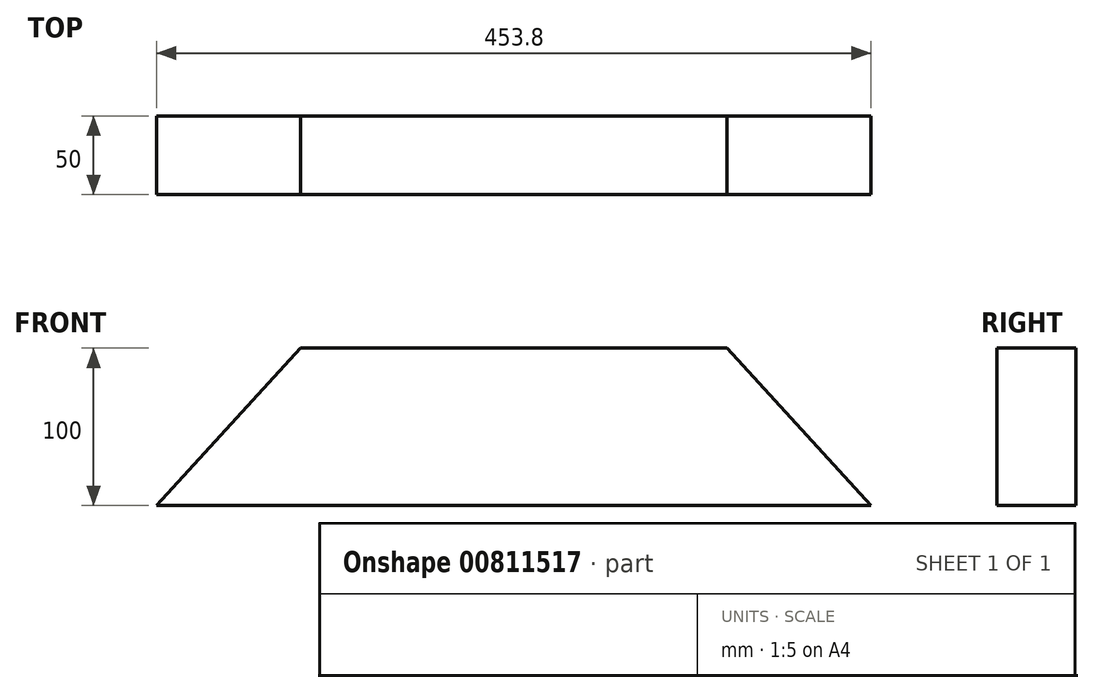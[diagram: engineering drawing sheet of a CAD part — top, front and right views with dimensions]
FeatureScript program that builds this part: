
annotation { "Feature Type Name" : "Feature", "Feature Type Description" : "" }
export const myFeature = defineFeature(function(context is Context, id is Id, definition is map)
    precondition{}
    {
        {
            var Q0;
            Q0=qCreatedBy(makeId("Front.planeOp"),FACE);
            var sketch = newSketch(context, id + "F0", { "sketchPlane" : qUnion([Q0])});
            skLineSegment(sketch, "E0", {"start": v(-1197.5, 0) * mm, "end": v(1197.5, 0) * mm, "construction": true});
            skLineSegment(sketch, "E1", {"start": v(1197.5, 0) * mm, "end": v(0, 1310) * mm, "construction": true});
            skLineSegment(sketch, "E2", {"start": v(0, 1310) * mm, "end": v(-1197.5, 0) * mm, "construction": true});
            skLineSegment(sketch, "E3", {"start": v(0, 1310) * mm, "end": v(-135.49, 1310) * mm, "construction": true});
            skLineSegment(sketch, "E4", {"start": v(-1197.5, 0) * mm, "end": v(-1332.99, 0) * mm, "construction": true});
            skLineSegment(sketch, "E5", {"start": v(-1332.99, 0) * mm, "end": v(-135.49, 1310) * mm, "construction": true});
            skLineSegment(sketch, "E6", {"start": v(-135.49, 1310) * mm, "end": v(135.49, 1310) * mm});
            skLineSegment(sketch, "E7", {"start": v(-135.49, 1310) * mm, "end": v(-226.9, 1210) * mm});
            skLineSegment(sketch, "E8", {"start": v(-226.9, 1210) * mm, "end": v(226.9, 1210) * mm});
            skLineSegment(sketch, "E9", {"start": v(226.9, 1210) * mm, "end": v(135.49, 1310) * mm});
            skPoint(sketch, "E10", {"position": v(0, 1210) * mm});
            skPoint(sketch, "E11", {"position": v(0, 1310) * mm});
            skSolve(sketch);
        }
        {
            var Q0;
            Q0=makeQuery(id+"F0.imprint","IMPRINT",FACE,{"disambiguationData":[TD([[makeQuery(id+"F0.imprint","IMPRINT",EDGE,{"derivedFrom":sQuery(id+"F0.wireOp",EDGE,"E6")}),-1.0]])]});
            extrude(context, id + "F1", {"entities" : qUnion([Q0]), "depth" : 50 * mm, "offsetDistance" : 25 * mm});
        }
    });
